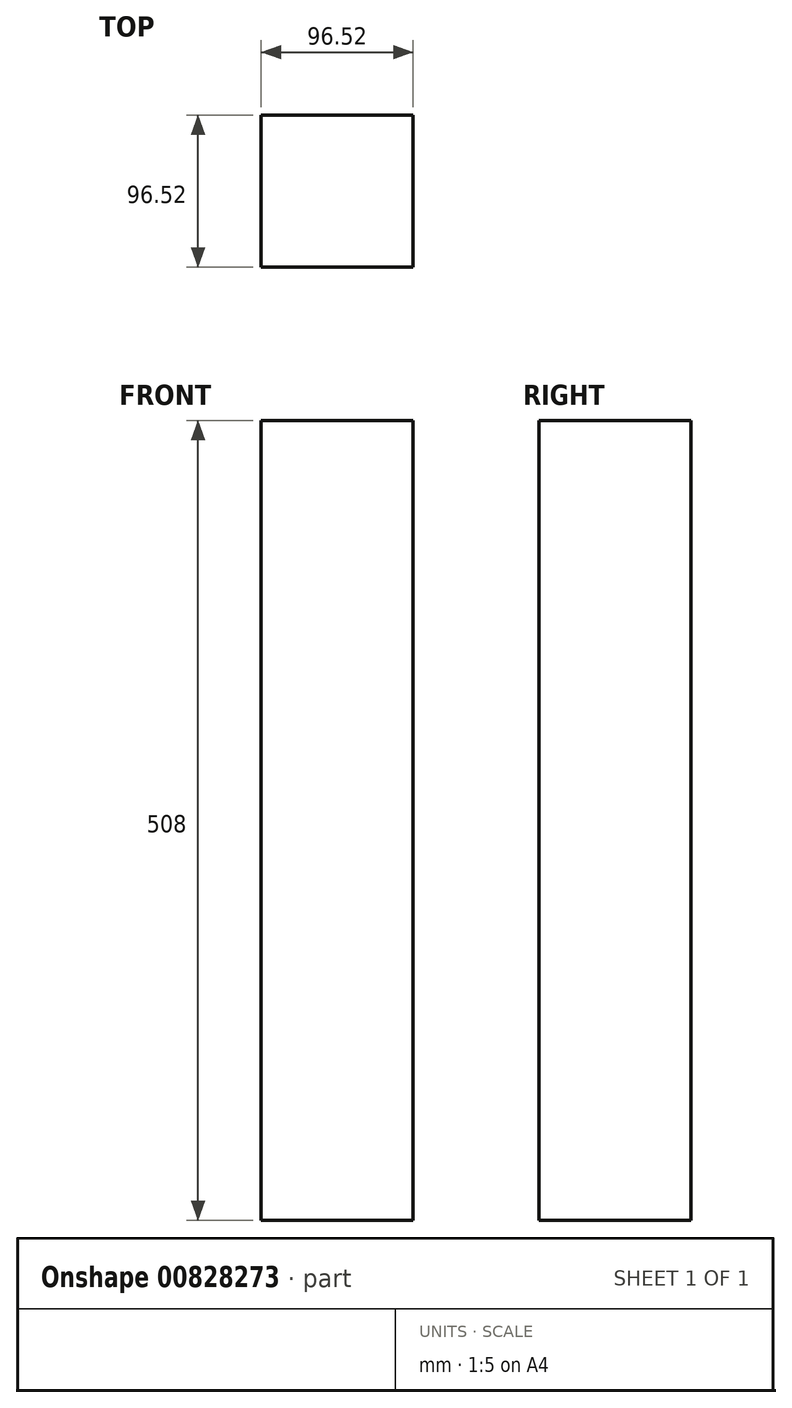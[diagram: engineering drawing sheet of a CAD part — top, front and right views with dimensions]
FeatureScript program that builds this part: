
annotation { "Feature Type Name" : "Feature", "Feature Type Description" : "" }
export const myFeature = defineFeature(function(context is Context, id is Id, definition is map)
    precondition{}
    {
        {
            var Q0;
            Q0=qCreatedBy(makeId("Top.planeOp"),FACE);
            var sketch = newSketch(context, id + "F0", { "sketchPlane" : qUnion([Q0])});
            skLineSegment(sketch, "E0.bottom", {"start": v(48.26, -48.26) * mm, "end": v(-48.26, -48.26) * mm});
            skLineSegment(sketch, "E0.top", {"start": v(48.26, 48.26) * mm, "end": v(-48.26, 48.26) * mm});
            skLineSegment(sketch, "E0.left", {"start": v(48.26, -48.26) * mm, "end": v(48.26, 48.26) * mm});
            skLineSegment(sketch, "E0.right", {"start": v(-48.26, -48.26) * mm, "end": v(-48.26, 48.26) * mm});
            skPoint(sketch, "E0.middle", {"position": v(0, 0) * mm});
            skSolve(sketch);
        }
        {
            var Q0;
            Q0 = qSketchRegion(id + "F0", true);
            extrude(context, id + "F1", {"entities" : qUnion([Q0]), "depth" : 508 * mm, "offsetDistance" : 25.4 * mm});
        }
    });
